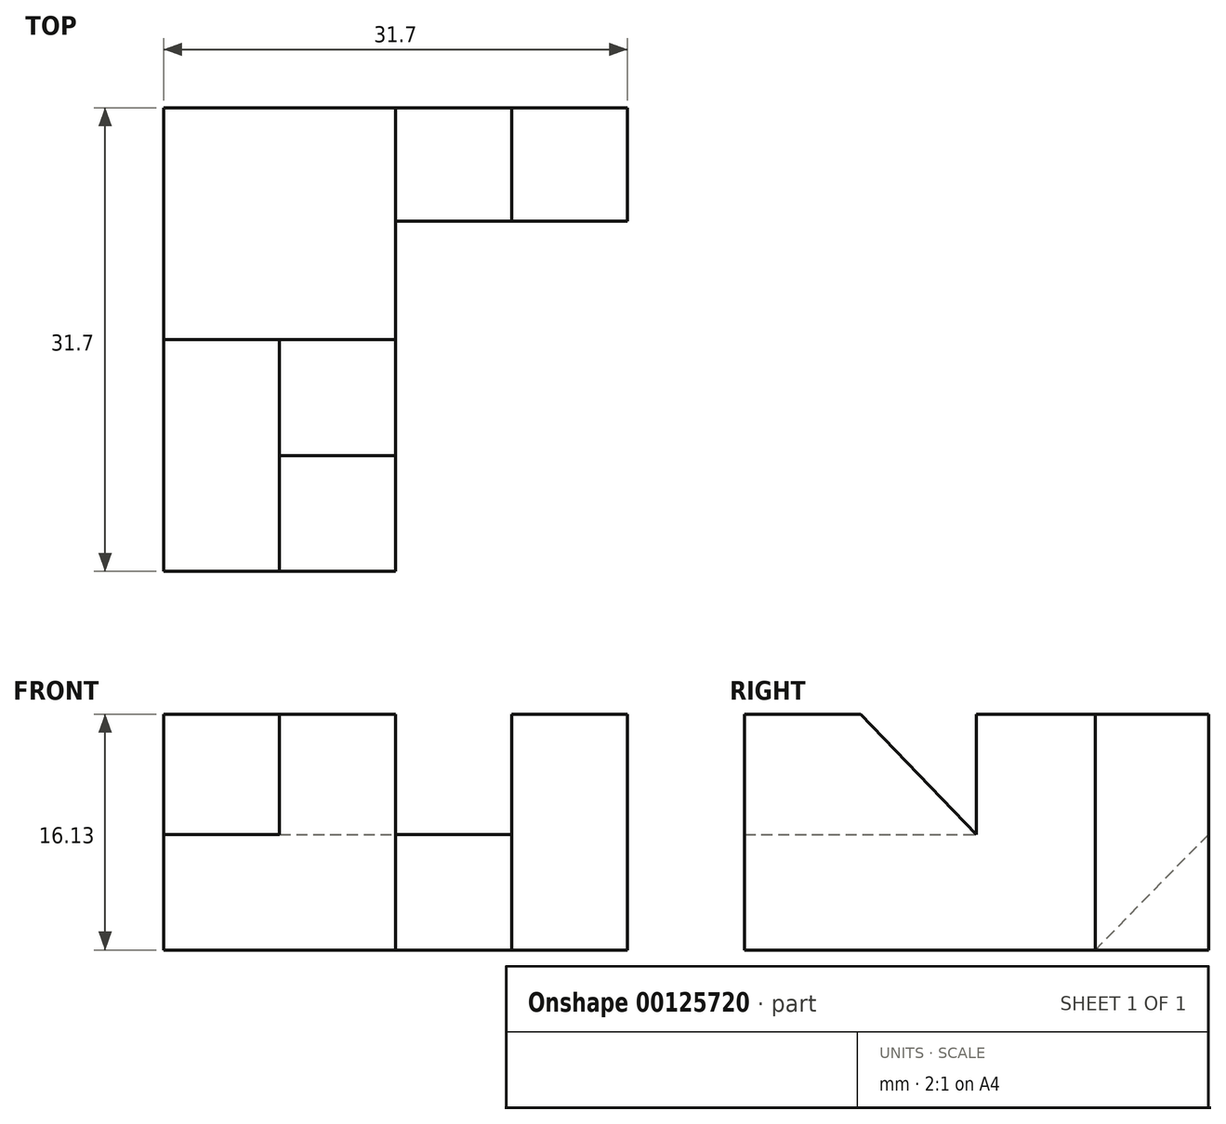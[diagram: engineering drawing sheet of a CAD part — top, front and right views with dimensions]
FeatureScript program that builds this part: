
annotation { "Feature Type Name" : "Feature", "Feature Type Description" : "" }
export const myFeature = defineFeature(function(context is Context, id is Id, definition is map)
    precondition{}
    {
        {
            var Q0;
            Q0=qCreatedBy(makeId("Top.planeOp"),FACE);
            var sketch = newSketch(context, id + "F0", { "sketchPlane" : qUnion([Q0])});
            skLineSegment(sketch, "E0", {"start": v(0, 0) * mm, "end": v(31.7, 0) * mm});
            skLineSegment(sketch, "E1", {"start": v(31.7, 0) * mm, "end": v(31.7, 31.7) * mm});
            skLineSegment(sketch, "E2", {"start": v(31.7, 31.7) * mm, "end": v(0, 31.7) * mm});
            skLineSegment(sketch, "E3", {"start": v(0, 31.7) * mm, "end": v(0, 0) * mm});
            skSolve(sketch);
        }
        {
            var Q0;
            Q0=makeQuery(id+"F0.imprint","IMPRINT",FACE,{"disambiguationData":[TD([[makeQuery(id+"F0.imprint","IMPRINT",EDGE,{"derivedFrom":sQuery(id+"F0.wireOp",EDGE,"E0")}),1.0]])]});
            extrude(context, id + "F1", {"entities" : qUnion([Q0]), "depth" : 7.9 * mm});
        }
        {
            var Q0;
            Q0=makeQuery(id+"F1.opExtrude","CAP_FACE",FACE,{"disambiguationData":[OSD([sQuery(id+"F0.wireOp",EDGE,"E0"),sQuery(id+"F0.wireOp",EDGE,"E1"),sQuery(id+"F0.wireOp",EDGE,"E2"),sQuery(id+"F0.wireOp",EDGE,"E3")])],"isStart":false});
            var sketch = newSketch(context, id + "F2", { "sketchPlane" : qUnion([Q0])});
            skLineSegment(sketch, "E4", {"start": v(31.7, 0) * mm, "end": v(31.7, 23.95) * mm});
            skLineSegment(sketch, "E5", {"start": v(15.85, 23.95) * mm, "end": v(15.85, 0) * mm});
            skLineSegment(sketch, "E6", {"start": v(15.85, 0) * mm, "end": v(31.7, 0) * mm});
            skLineSegment(sketch, "E7", {"start": v(31.7, 23.95) * mm, "end": v(15.85, 23.95) * mm});
            skLineSegment(sketch, "E8", {"start": v(23.78, 23.95) * mm, "end": v(23.78, 31.7) * mm});
            skLineSegment(sketch, "E9", {"start": v(23.78, 31.7) * mm, "end": v(31.7, 31.7) * mm});
            skLineSegment(sketch, "E10", {"start": v(31.7, 31.7) * mm, "end": v(31.7, 23.95) * mm});
            skLineSegment(sketch, "E11", {"start": v(23.78, 23.95) * mm, "end": v(31.7, 23.95) * mm});
            skSolve(sketch);
        }
        {
            var Q0;
            Q0=makeQuery(id+"F2.imprint","IMPRINT",FACE,{"disambiguationData":[TD([[makeQuery(id+"F2.imprint","IMPRINT",EDGE,{"derivedFrom":sQuery(id+"F2.wireOp",EDGE,"E4")}),1.0]])]});
            extrude(context, id + "F3", {"entities" : qUnion([Q0]), "operationType" : NewBodyOperationType.REMOVE, "endBound" : BoundingType.THROUGH_ALL, "oppositeDirection" : true, "depth" : 25 * mm});
        }
        {
            var Q0;
            Q0=makeQuery(id+"F1.opExtrude","CAP_FACE",FACE,{"disambiguationData":[OSD([sQuery(id+"F0.wireOp",EDGE,"E0"),sQuery(id+"F0.wireOp",EDGE,"E1"),sQuery(id+"F0.wireOp",EDGE,"E2"),sQuery(id+"F0.wireOp",EDGE,"E3")])],"isStart":false});
            var sketch = newSketch(context, id + "F4", { "sketchPlane" : qUnion([Q0])});
            skLineSegment(sketch, "E12.0.0", {"start": v(23.78, 31.7) * mm, "end": v(23.78, 23.95) * mm});
            skLineSegment(sketch, "E12.0.1", {"start": v(23.78, 23.95) * mm, "end": v(31.7, 23.95) * mm});
            skLineSegment(sketch, "E12.0.2", {"start": v(31.7, 23.95) * mm, "end": v(31.7, 31.7) * mm});
            skLineSegment(sketch, "E12.0.3", {"start": v(31.7, 31.7) * mm, "end": v(23.78, 31.7) * mm});
            skSolve(sketch);
        }
        {
            var Q0;
            Q0=qSketchRegion(id+"F4",true);
            var Q1;
            Q1=makeQuery(id+"F2.imprint","IMPRINT",FACE,{"disambiguationData":[TD([[makeQuery(id+"F2.imprint","IMPRINT",EDGE,{"derivedFrom":sQuery(id+"F2.wireOp",EDGE,"E8")}),-1.0]])]});
            extrude(context, id + "F5", {"entities" : qUnion([Q0, Q1]), "operationType" : NewBodyOperationType.ADD, "depth" : 8.23 * mm});
        }
        {
            var Q0;
            {var subQ3=sQuery(id+"F2.wireOp",EDGE,"E5");Q0=makeQuery(id+"F2.imprint","IMPRINT",FACE,{"disambiguationData":[TD([[makeQuery(id+"F2.imprint","IMPRINT",EDGE,{"derivedFrom":subQ3}),-1.0]])]});}
            extrude(context, id + "F6", {"entities" : qUnion([Q0]), "operationType" : NewBodyOperationType.ADD, "depth" : 8.23 * mm});
        }
        {
            var Q0;
            {var subQ0=sQuery(id+"F2.wireOp",EDGE,"E8");Q0=makeQuery(id+"F6.boolean.opBoolean","MERGE",FACE,{"derivedFrom":[makeQuery(id+"F5.opExtrude","CAP_FACE",FACE,{"disambiguationData":[OSD([subQ0,sQuery(id+"F2.wireOp",EDGE,"E9"),sQuery(id+"F2.wireOp",EDGE,"E10"),sQuery(id+"F2.wireOp",EDGE,"E11")])],"isStart":false}),makeQuery(id+"F6.opExtrude","CAP_FACE",FACE,{"disambiguationData":[OSD([sQuery(id+"F0.wireOp",EDGE,"E0"),sQuery(id+"F0.wireOp",EDGE,"E2"),sQuery(id+"F0.wireOp",EDGE,"E3"),sQuery(id+"F2.wireOp",EDGE,"E5"),sQuery(id+"F2.wireOp",EDGE,"E7"),subQ0])],"isStart":false})]});}
            var sketch = newSketch(context, id + "F7", { "sketchPlane" : qUnion([Q0])});
            skLineSegment(sketch, "E13", {"start": v(7.93, 0) * mm, "end": v(7.93, 7.92) * mm});
            skLineSegment(sketch, "E14", {"start": v(7.93, 7.92) * mm, "end": v(15.85, 7.92) * mm});
            skLineSegment(sketch, "E15", {"start": v(15.85, 7.92) * mm, "end": v(15.85, 0) * mm});
            skLineSegment(sketch, "E16", {"start": v(15.85, 0) * mm, "end": v(7.93, 0) * mm});
            skLineSegment(sketch, "E17", {"start": v(15.85, 31.7) * mm, "end": v(0, 31.7) * mm});
            skLineSegment(sketch, "E18", {"start": v(0, 31.7) * mm, "end": v(0, 15.85) * mm});
            skLineSegment(sketch, "E19", {"start": v(0, 15.85) * mm, "end": v(15.85, 15.85) * mm});
            skLineSegment(sketch, "E20", {"start": v(15.85, 15.85) * mm, "end": v(15.85, 31.7) * mm});
            skLineSegment(sketch, "E21", {"start": v(31.7, 31.7) * mm, "end": v(31.7, 23.95) * mm});
            skLineSegment(sketch, "E22", {"start": v(31.7, 23.95) * mm, "end": v(23.78, 23.95) * mm});
            skLineSegment(sketch, "E23", {"start": v(23.78, 23.95) * mm, "end": v(23.78, 31.7) * mm});
            skLineSegment(sketch, "E24", {"start": v(23.78, 31.7) * mm, "end": v(31.7, 31.7) * mm});
            skSolve(sketch);
        }
        {
            var Q0;
            {var subQ5=sQuery(id+"F7.wireOp",EDGE,"E23");Q0=makeQuery(id+"F7.imprint","IMPRINT",FACE,{"disambiguationData":[TD([[makeQuery(id+"F7.imprint","IMPRINT",EDGE,{"derivedFrom":subQ5}),1.0]])]});}
            var Q1;
            {var subQ3=sQuery(id+"F7.wireOp",EDGE,"E13");Q1=makeQuery(id+"F7.imprint","IMPRINT",FACE,{"disambiguationData":[TD([[makeQuery(id+"F7.imprint","IMPRINT",EDGE,{"derivedFrom":subQ3}),1.0]])]});}
            extrude(context, id + "F8", {"entities" : qUnion([Q0, Q1]), "operationType" : NewBodyOperationType.REMOVE, "oppositeDirection" : true, "depth" : 8.23 * mm});
        }
        {
            var Q0;
            {var subQ0=sQuery(id+"F2.wireOp",EDGE,"E5");Q0=makeQuery(id+"F8.boolean.opBoolean","MERGE",FACE,{"derivedFrom":[makeQuery(id+"F6.boolean.opBoolean","MERGE",FACE,{"derivedFrom":[makeQuery(id+"F3.boolean.opBoolean","COPY",FACE,{"derivedFrom":makeQuery(id+"F3.opExtrude","SWEPT_FACE",FACE,{"disambiguationData":[OSD([subQ0])]})}),makeQuery(id+"F6.opExtrude","SWEPT_FACE",FACE,{"disambiguationData":[OSD([subQ0])]})]}),makeQuery(id+"F8.opExtrude","SWEPT_FACE",FACE,{"disambiguationData":[OSD([sQuery(id+"F7.wireOp",EDGE,"E20")])]})]});}
            var sketch = newSketch(context, id + "F9", { "sketchPlane" : qUnion([Q0])});
            skLineSegment(sketch, "E25", {"start": v(7.92, 16.13) * mm, "end": v(15.85, 7.9) * mm});
            skLineSegment(sketch, "E26.0", {"start": v(0, 16.13) * mm, "end": v(7.92, 16.13) * mm});
            skLineSegment(sketch, "E27.0", {"start": v(7.92, 7.9) * mm, "end": v(7.92, 16.13) * mm});
            skLineSegment(sketch, "E28", {"start": v(7.92, 7.9) * mm, "end": v(15.85, 7.9) * mm});
            skSolve(sketch);
        }
        {
            var Q0;
            Q0=makeQuery(id+"F9.imprint","IMPRINT",FACE,{"disambiguationData":[TD([[makeQuery(id+"F9.imprint","IMPRINT",EDGE,{"derivedFrom":sQuery(id+"F9.wireOp",EDGE,"E25")}),-1.0]])]});
            var Q1;
            Q1=makeQuery(id+"F8.boolean.opBoolean","COPY",FACE,{"derivedFrom":makeQuery(id+"F8.opExtrude","SWEPT_FACE",FACE,{"disambiguationData":[OSD([sQuery(id+"F7.wireOp",EDGE,"E13")])]})});
            extrude(context, id + "F10", {"entities" : qUnion([Q0]), "operationType" : NewBodyOperationType.ADD, "endBound" : BoundingType.UP_TO_SURFACE, "oppositeDirection" : true, "endBoundEntityFace" : qUnion([Q1]), "depth" : 25 * mm});
        }
        {
            var Q0;
            {var subQ0=sQuery(id+"F2.wireOp",EDGE,"E5");Q0=makeQuery(id+"F10.boolean.opBoolean","MERGE",FACE,{"derivedFrom":[makeQuery(id+"F8.boolean.opBoolean","MERGE",FACE,{"derivedFrom":[makeQuery(id+"F6.boolean.opBoolean","MERGE",FACE,{"derivedFrom":[makeQuery(id+"F3.boolean.opBoolean","COPY",FACE,{"derivedFrom":makeQuery(id+"F3.opExtrude","SWEPT_FACE",FACE,{"disambiguationData":[OSD([subQ0])]})}),makeQuery(id+"F6.opExtrude","SWEPT_FACE",FACE,{"disambiguationData":[OSD([subQ0])]})]}),makeQuery(id+"F8.opExtrude","SWEPT_FACE",FACE,{"disambiguationData":[OSD([sQuery(id+"F7.wireOp",EDGE,"E20")])]})]}),makeQuery(id+"F10.opExtrude","CAP_FACE",FACE,{"disambiguationData":[OSD([sQuery(id+"F9.wireOp",EDGE,"E25"),sQuery(id+"F9.wireOp",EDGE,"E27.0"),sQuery(id+"F9.wireOp",EDGE,"E28")])],"isStart":true})]});}
            var sketch = newSketch(context, id + "F11", { "sketchPlane" : qUnion([Q0])});
            skLineSegment(sketch, "E29", {"start": v(31.7, 7.9) * mm, "end": v(23.95, 0) * mm});
            skLineSegment(sketch, "E30", {"start": v(23.95, 0) * mm, "end": v(23.95, 7.9) * mm});
            skLineSegment(sketch, "E31", {"start": v(23.95, 7.9) * mm, "end": v(31.7, 7.9) * mm});
            skSolve(sketch);
        }
        {
            var Q0;
            Q0=qSketchRegion(id+"F11",true);
            var Q1;
            Q1=makeQuery(id+"F8.boolean.opBoolean","COPY",FACE,{"derivedFrom":makeQuery(id+"F8.opExtrude","SWEPT_FACE",FACE,{"disambiguationData":[OSD([sQuery(id+"F7.wireOp",EDGE,"E23")])]})});
            extrude(context, id + "F12", {"entities" : qUnion([Q0]), "operationType" : NewBodyOperationType.REMOVE, "endBound" : BoundingType.UP_TO_SURFACE, "endBoundEntityFace" : qUnion([Q1]), "depth" : 25 * mm});
        }
    });
